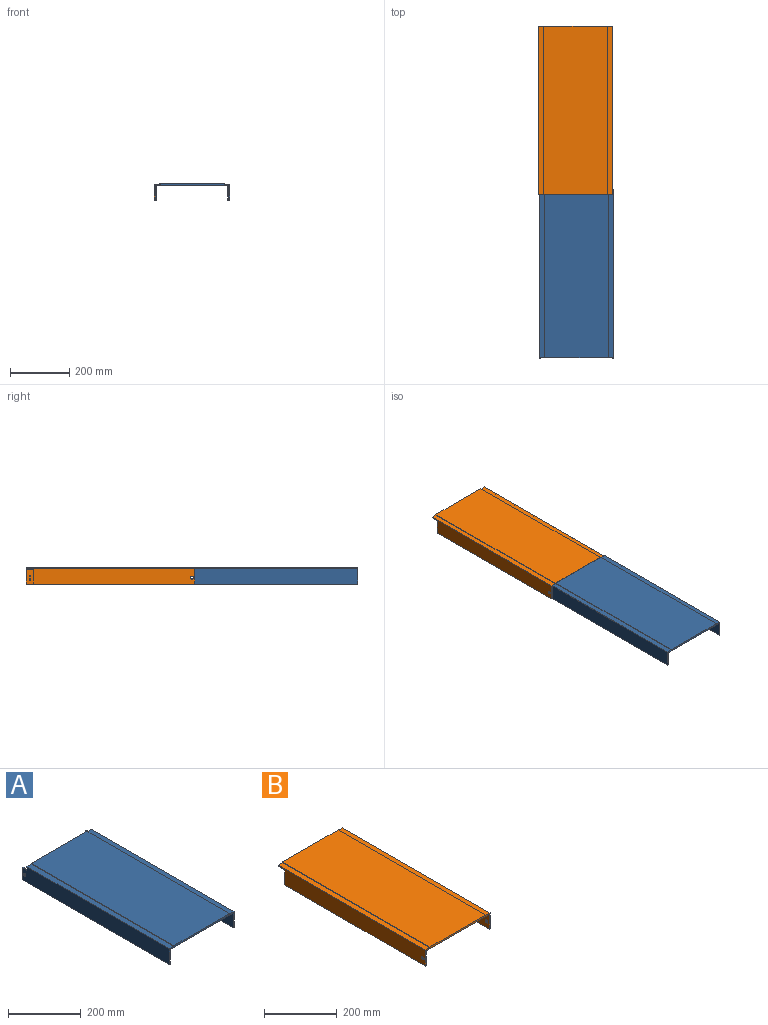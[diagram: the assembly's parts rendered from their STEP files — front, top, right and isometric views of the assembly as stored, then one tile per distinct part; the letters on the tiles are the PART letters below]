
ASSEMBLY  parts=2 mates=1
PART A: 20 faces, bbox 250.8x571.5x55.2 mm
  f0: plane 552.45x17.78mm, normal (0,0,1), area 9822.6mm2, adj f1,f12,f14,f16
  f1: plane 552.45x1.91mm, normal (1,0,0), area 1052.4mm2, adj f0,f2,f14,f16
  f2: plane 552.45x215.27mm, normal (0,0,1), area 118923.1mm2, adj f1,f3,f14,f16
  f3: plane 552.45x1.91mm, normal (-1,0,0), area 1052.4mm2, adj f2,f4,f14,f16
  f4: plane 552.45x17.78mm, normal (0,0,1), area 9822.6mm2, adj f3,f5,f14,f16
  f5: plane 571.5x53.34mm, normal (-1,0,0), area 30170.6mm2, adj f4,f9,f10,f14,f16,f17,f19
  f6: plane 571.5x50.17mm, normal (1,0,0), area 28416.6mm2, adj f7,f9,f10,f14,f16,f17,f19
  f7: plane 552.45x244.48mm, normal (0,0,-1), area 135060.2mm2, adj f6,f8,f14,f16
  f8: plane 571.5x50.17mm, normal (-1,0,0), area 28416.6mm2, adj f7,f11,f13,f14,f15,f16,f18
  f9: plane 40.64x3.18mm, normal (0,1,0), area 129mm2, adj f5,f6,f10,f17
  f10: plane 571.5x3.18mm, normal (0,0,-1), area 1814.5mm2, adj f5,f6,f9,f14
  f11: plane 571.5x3.18mm, normal (0,0,-1), area 1814.5mm2, adj f8,f12,f13,f14
  f12: plane 571.5x53.34mm, normal (1,0,0), area 30170.6mm2, adj f0,f11,f13,f14,f15,f16,f18
  f13: plane 40.64x3.18mm, normal (0,1,0), area 129mm2, adj f8,f11,f12,f18
  f14: plane 250.83x55.25mm, normal (0,-1,0), area 1525mm2, adj f0,f1,f2,f3,f4,f5,f6,f7
  f15: cylinder r=4.76mm len=9.53mm, axis (1,0,0), area 95mm2, adj f8,f12
  f16: plane 250.83x14.61mm, normal (0,1,0), area 1266.9mm2, adj f0,f1,f2,f3,f4,f5,f6,f7
  f17: plane 19.05x3.18mm, normal (0,0,1), area 60.5mm2, adj f5,f6,f9,f16
  f18: plane 19.05x3.18mm, normal (0,0,1), area 60.5mm2, adj f8,f12,f13,f16
  f19: cylinder r=4.76mm len=9.53mm, axis (1,0,0), area 95mm2, adj f5,f6
PART B: 22 faces, bbox 250.8x571.5x55.2 mm
  f0: plane 546.1x3.18mm, normal (0,0,-1), area 1733.9mm2, adj f1,f7,f13,f21
  f1: plane 546.1x50.17mm, normal (1,0,0), area 27323.9mm2, adj f0,f8,f13,f15,f21
  f2: plane 571.5x17.78mm, normal (0,0,1), area 10161.3mm2, adj f3,f11,f12,f13
  f3: plane 571.5x1.91mm, normal (1,0,0), area 1088.7mm2, adj f2,f4,f12,f13
  f4: plane 571.5x215.27mm, normal (0,0,1), area 123023.9mm2, adj f3,f5,f12,f13
  f5: plane 571.5x1.91mm, normal (-1,0,0), area 1088.7mm2, adj f4,f6,f12,f13
  f6: plane 571.5x17.78mm, normal (0,0,1), area 10161.3mm2, adj f5,f7,f12,f13
  f7: plane 571.5x53.34mm, normal (-1,0,0), area 29138.4mm2, adj f0,f6,f8,f12,f13,f15,f21
  f8: plane 571.5x247.65mm, normal (0,0,-1), area 139798.1mm2, adj f1,f7,f9,f12,f13,f21
  f9: plane 571.5x50.17mm, normal (-1,0,0), area 28496.7mm2, adj f8,f10,f12,f13,f14,f16,f17,f18
  f10: plane 571.5x3.18mm, normal (0,0,-1), area 1814.5mm2, adj f9,f11,f12,f13
  f11: plane 571.5x53.34mm, normal (1,0,0), area 30311.2mm2, adj f2,f10,f12,f13,f14,f16,f17,f18
  f12: plane 250.83x55.25mm, normal (0,1,0), area 1365.7mm2, adj f2,f3,f4,f5,f6,f7,f8,f9
  f13: plane 250.83x55.25mm, normal (0,-1,0), area 1525mm2, adj f0,f1,f2,f3,f4,f5,f6,f7
  f14: cylinder r=4.76mm len=9.53mm, axis (1,0,0), area 95mm2, adj f9,f11
  f15: cylinder r=4.76mm len=9.53mm, axis (1,0,0), area 95mm2, adj f1,f7
  f16: cylinder r=2.54mm len=5.08mm, axis (1,0,0), area 50.7mm2, adj f9,f11
  f17: cylinder r=2.54mm len=5.08mm, axis (1,0,0), area 50.7mm2, adj f9,f11
  f18: cylinder r=2.54mm len=5.08mm, axis (1,0,0), area 50.7mm2, adj f9,f11
  f19: cylinder r=2.54mm len=5.08mm, axis (1,0,0), area 50.7mm2, adj f9,f11
  f20: cylinder r=2.54mm len=5.08mm, axis (1,0,0), area 50.7mm2, adj f9,f11
  f21: plane 50.17x3.18mm, normal (0,1,0), area 159.3mm2, adj f0,f1,f7,f8
PLACE A t=(135.14,791.38,-166)mm
PLACE B t=(487.57,1343.83,-166)mm
MATE revolute A.f15 <-> B.f14  axis (-1,0,0) through (738.39,1353.36,-144.41)mm
